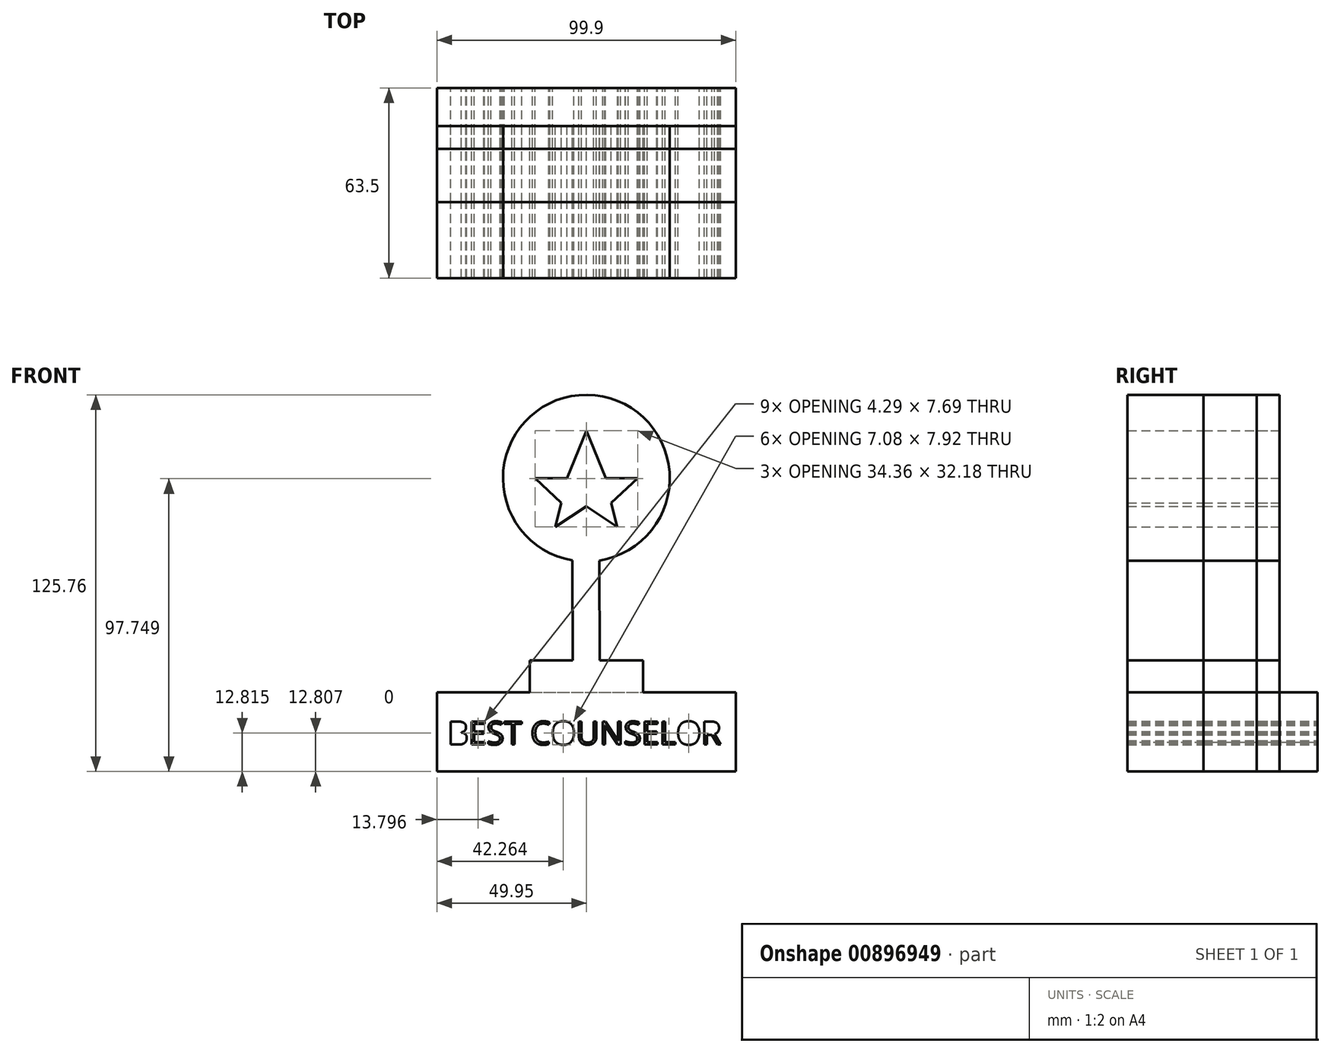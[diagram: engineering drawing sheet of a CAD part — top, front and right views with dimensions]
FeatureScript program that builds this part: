
annotation { "Feature Type Name" : "Feature", "Feature Type Description" : "" }
export const myFeature = defineFeature(function(context is Context, id is Id, definition is map)
    precondition{}
    {
        {
            var Q0;
            Q0=qCreatedBy(makeId("Front.planeOp"),FACE);
            var sketch = newSketch(context, id + "F0", { "sketchPlane" : qUnion([Q0])});
            skArc(sketch, "E0", {"start": v(4.31, 5.18) * mm, "mid": v(0.22, 60.55) * mm, "end": v(-4.75, 5.25) * mm});
            skLineSegment(sketch, "E1.left", {"start": v(-4.75, 5.25) * mm, "end": v(-4.58, -28.13) * mm});
            skLineSegment(sketch, "E1.right", {"start": v(4.31, 5.18) * mm, "end": v(4.48, -28.13) * mm});
            skLineSegment(sketch, "E2.top", {"start": v(-18.91, -28.13) * mm, "end": v(-4.58, -28.13) * mm});
            skLineSegment(sketch, "E2.left", {"start": v(-18.91, -38.77) * mm, "end": v(-18.91, -28.13) * mm});
            skLineSegment(sketch, "E2.right", {"start": v(18.91, -38.77) * mm, "end": v(18.91, -28.13) * mm});
            skLineSegment(sketch, "E3.bottom", {"start": v(-49.95, -38.77) * mm, "end": v(-18.91, -38.77) * mm});
            skLineSegment(sketch, "E3.top", {"start": v(-49.95, -65.21) * mm, "end": v(49.95, -65.21) * mm});
            skLineSegment(sketch, "E3.left", {"start": v(-49.95, -38.77) * mm, "end": v(-49.95, -65.21) * mm});
            skLineSegment(sketch, "E3.right", {"start": v(49.95, -38.77) * mm, "end": v(49.95, -65.21) * mm});
            skPoint(sketch, "E3.middle", {"position": v(0, -52) * mm});
            skLineSegment(sketch, "E4", {"start": v(-122.13, 13.32) * mm, "end": v(-124.07, 16.07) * mm});
            skText(sketch, "E5", { "text": "BEST COUNSELOR\n", "fontName": "OpenSans-Regular.ttf"});
            skLineSegment(sketch, "E6", {"start": v(0, 48.63) * mm, "end": v(6.5, 32.7) * mm});
            skLineSegment(sketch, "E7", {"start": v(6.5, 32.7) * mm, "end": v(17.18, 32.7) * mm});
            skLineSegment(sketch, "E8", {"start": v(17.18, 32.7) * mm, "end": v(8.33, 24.5) * mm});
            skLineSegment(sketch, "E9", {"start": v(8.33, 24.5) * mm, "end": v(10.34, 16.45) * mm});
            skLineSegment(sketch, "E10", {"start": v(0, 60.55) * mm, "end": v(0, 3.64) * mm, "construction": true});
            skPoint(sketch, "E11.start.orphan", {"position": v(-7.83, 32.7) * mm});
            skLineSegment(sketch, "E12.trimOffspring", {"start": v(0, 23.34) * mm, "end": v(10.34, 16.45) * mm});
            skLineSegment(sketch, "E13.MirrorCS", {"start": v(0, 48.63) * mm, "end": v(-6.5, 32.7) * mm});
            skLineSegment(sketch, "E14.MirrorCS", {"start": v(-6.5, 32.7) * mm, "end": v(-17.18, 32.7) * mm});
            skLineSegment(sketch, "E15.MirrorCS", {"start": v(-17.18, 32.7) * mm, "end": v(-8.33, 24.5) * mm});
            skLineSegment(sketch, "E16.MirrorCS", {"start": v(-8.33, 24.5) * mm, "end": v(-10.34, 16.45) * mm});
            skLineSegment(sketch, "E17.MirrorCS", {"start": v(0, 23.34) * mm, "end": v(-10.34, 16.45) * mm});
            skLineSegment(sketch, "E18.trimOffspring", {"start": v(4.48, -28.13) * mm, "end": v(18.91, -28.13) * mm});
            skLineSegment(sketch, "E19.trimOffspring", {"start": v(18.91, -38.77) * mm, "end": v(49.95, -38.77) * mm});
            skLineSegment(sketch, "E20", {"start": v(-4.75, 5.25) * mm, "end": v(4.31, 5.18) * mm});
            skLineSegment(sketch, "E21", {"start": v(-4.58, -28.13) * mm, "end": v(4.48, -28.13) * mm});
            skLineSegment(sketch, "E22", {"start": v(-18.91, -38.77) * mm, "end": v(18.91, -38.77) * mm});
            const initialGuessF0  = {"E5": [-0.04634, -0.05625, 1, 0, 0.00776]};
            skSetInitialGuess(sketch, initialGuessF0);
            skSolve(sketch);
        }
        {
            var Q0;
            Q0=makeQuery(id+"F0.imprint","IMPRINT",FACE,{"disambiguationData":[TD([[makeQuery(id+"F0.imprint","IMPRINT",EDGE,{"derivedFrom":sQuery(id+"F0.wireOp",EDGE,"E3.top")}),1.0]])]});
            extrude(context, id + "F1", {"entities" : qUnion([Q0]), "endBound" : BoundingType.SYMMETRIC, "depth" : 25.4 * mm, "offsetDistance" : 25.4 * mm});
        }
        {
            var Q0;
            Q0=makeQuery(id+"F0.imprint","IMPRINT",FACE,{"disambiguationData":[TD([[makeQuery(id+"F0.imprint","IMPRINT",EDGE,{"derivedFrom":sQuery(id+"F0.wireOp",EDGE,"E2.top")}),-1.0]])]});
            var Q1;
            Q1=makeQuery(id+"F0.imprint","IMPRINT",FACE,{"disambiguationData":[TD([[makeQuery(id+"F0.imprint","IMPRINT",EDGE,{"derivedFrom":sQuery(id+"F0.wireOp",EDGE,"E1.top")}),1.0]])]});
            var Q2;
            Q2=makeQuery(id+"F0.imprint","IMPRINT",FACE,{"disambiguationData":[TD([[makeQuery(id+"F0.imprint","IMPRINT",EDGE,{"derivedFrom":sQuery(id+"F0.wireOp",EDGE,"E6")}),1.0]])]});
            extrude(context, id + "F2", {"entities" : qUnion([Q0, Q1, Q2]), "operationType" : NewBodyOperationType.ADD, "depth" : 12.7 * mm, "offsetDistance" : 25.4 * mm});
        }
        {
            var Q0;
            Q0=makeQuery(id+"F0.imprint","IMPRINT",FACE,{"disambiguationData":[TD([[makeQuery(id+"F0.imprint","IMPRINT",EDGE,{"derivedFrom":sQuery(id+"F0.wireOp",EDGE,"E0")}),1.0]])]});
            extrude(context, id + "F3", {"entities" : qUnion([Q0]), "operationType" : NewBodyOperationType.ADD, "depth" : 25.4 * mm, "offsetDistance" : 25.4 * mm});
        }
        {
            var Q0;
            Q0=qCreatedBy(makeId("Front.planeOp"),FACE);
            var sketch = newSketch(context, id + "F4", { "sketchPlane" : qUnion([Q0])});
            skSolve(sketch);
        }
        {
            var Q0;
            Q0 = qSketchRegion(id + "F4", true);
            var Q1;
            Q1 = qSketchRegion(id + "F0", true);
            extrude(context, id + "F5", {"entities" : qUnion([Q0, Q1]), "operationType" : NewBodyOperationType.ADD, "depth" : 25.4 * mm, "offsetDistance" : 25.4 * mm});
        }
        {
            var Q0;
            Q0 = qSketchRegion(id + "F0", true);
            extrude(context, id + "F6", {"entities" : qUnion([Q0]), "depth" : 7.62 * mm, "offsetDistance" : 25.4 * mm});
        }
        {
            var Q0;
            Q0=makeQuery(id+"F5.opExtrude","CAP_FACE",FACE,{"disambiguationData":[OSD([sQuery(id+"F0.wireOp",EDGE,"E0"),sQuery(id+"F0.wireOp",EDGE,"E1.left"),sQuery(id+"F0.wireOp",EDGE,"E1.right"),sQuery(id+"F0.wireOp",EDGE,"E2.top"),sQuery(id+"F0.wireOp",EDGE,"E2.left"),sQuery(id+"F0.wireOp",EDGE,"E2.right"),sQuery(id+"F0.wireOp",EDGE,"E3.bottom"),sQuery(id+"F0.wireOp",EDGE,"E3.top"),sQuery(id+"F0.wireOp",EDGE,"E3.left"),sQuery(id+"F0.wireOp",EDGE,"E3.right"),sQuery(id+"F0.wireOp",EDGE,"E5.sketch_text.stroke-0"),sQuery(id+"F0.wireOp",EDGE,"E5.sketch_text.stroke-1"),sQuery(id+"F0.wireOp",EDGE,"E5.sketch_text.stroke-2"),sQuery(id+"F0.wireOp",EDGE,"E5.sketch_text.stroke-3"),sQuery(id+"F0.wireOp",EDGE,"E5.sketch_text.stroke-4"),sQuery(id+"F0.wireOp",EDGE,"E5.sketch_text.stroke-5"),sQuery(id+"F0.wireOp",EDGE,"E5.sketch_text.stroke-6"),sQuery(id+"F0.wireOp",EDGE,"E5.sketch_text.stroke-7"),sQuery(id+"F0.wireOp",EDGE,"E5.sketch_text.stroke-8"),sQuery(id+"F0.wireOp",EDGE,"E5.sketch_text.stroke-9"),sQuery(id+"F0.wireOp",EDGE,"E5.sketch_text.stroke-10"),sQuery(id+"F0.wireOp",EDGE,"E5.sketch_text.stroke-25"),sQuery(id+"F0.wireOp",EDGE,"E5.sketch_text.stroke-26"),sQuery(id+"F0.wireOp",EDGE,"E5.sketch_text.stroke-27"),sQuery(id+"F0.wireOp",EDGE,"E5.sketch_text.stroke-28"),sQuery(id+"F0.wireOp",EDGE,"E5.sketch_text.stroke-29"),sQuery(id+"F0.wireOp",EDGE,"E5.sketch_text.stroke-30"),sQuery(id+"F0.wireOp",EDGE,"E5.sketch_text.stroke-31"),sQuery(id+"F0.wireOp",EDGE,"E5.sketch_text.stroke-32"),sQuery(id+"F0.wireOp",EDGE,"E5.sketch_text.stroke-33"),sQuery(id+"F0.wireOp",EDGE,"E5.sketch_text.stroke-34"),sQuery(id+"F0.wireOp",EDGE,"E5.sketch_text.stroke-35"),sQuery(id+"F0.wireOp",EDGE,"E5.sketch_text.stroke-36"),sQuery(id+"F0.wireOp",EDGE,"E5.sketch_text.stroke-37"),sQuery(id+"F0.wireOp",EDGE,"E5.sketch_text.stroke-38"),sQuery(id+"F0.wireOp",EDGE,"E5.sketch_text.stroke-39"),sQuery(id+"F0.wireOp",EDGE,"E5.sketch_text.stroke-40"),sQuery(id+"F0.wireOp",EDGE,"E5.sketch_text.stroke-41"),sQuery(id+"F0.wireOp",EDGE,"E5.sketch_text.stroke-42"),sQuery(id+"F0.wireOp",EDGE,"E5.sketch_text.stroke-43"),sQuery(id+"F0.wireOp",EDGE,"E5.sketch_text.stroke-44"),sQuery(id+"F0.wireOp",EDGE,"E5.sketch_text.stroke-45"),sQuery(id+"F0.wireOp",EDGE,"E5.sketch_text.stroke-46"),sQuery(id+"F0.wireOp",EDGE,"E5.sketch_text.stroke-47"),sQuery(id+"F0.wireOp",EDGE,"E5.sketch_text.stroke-48"),sQuery(id+"F0.wireOp",EDGE,"E5.sketch_text.stroke-49"),sQuery(id+"F0.wireOp",EDGE,"E5.sketch_text.stroke-50"),sQuery(id+"F0.wireOp",EDGE,"E5.sketch_text.stroke-51"),sQuery(id+"F0.wireOp",EDGE,"E5.sketch_text.stroke-52"),sQuery(id+"F0.wireOp",EDGE,"E5.sketch_text.stroke-53"),sQuery(id+"F0.wireOp",EDGE,"E5.sketch_text.stroke-54"),sQuery(id+"F0.wireOp",EDGE,"E5.sketch_text.stroke-55"),sQuery(id+"F0.wireOp",EDGE,"E5.sketch_text.stroke-56"),sQuery(id+"F0.wireOp",EDGE,"E5.sketch_text.stroke-57"),sQuery(id+"F0.wireOp",EDGE,"E5.sketch_text.stroke-58"),sQuery(id+"F0.wireOp",EDGE,"E5.sketch_text.stroke-59"),sQuery(id+"F0.wireOp",EDGE,"E5.sketch_text.stroke-60"),sQuery(id+"F0.wireOp",EDGE,"E5.sketch_text.stroke-61"),sQuery(id+"F0.wireOp",EDGE,"E5.sketch_text.stroke-62"),sQuery(id+"F0.wireOp",EDGE,"E5.sketch_text.stroke-63"),sQuery(id+"F0.wireOp",EDGE,"E5.sketch_text.stroke-64"),sQuery(id+"F0.wireOp",EDGE,"E5.sketch_text.stroke-65"),sQuery(id+"F0.wireOp",EDGE,"E5.sketch_text.stroke-66"),sQuery(id+"F0.wireOp",EDGE,"E5.sketch_text.stroke-67"),sQuery(id+"F0.wireOp",EDGE,"E5.sketch_text.stroke-68"),sQuery(id+"F0.wireOp",EDGE,"E5.sketch_text.stroke-69"),sQuery(id+"F0.wireOp",EDGE,"E5.sketch_text.stroke-70"),sQuery(id+"F0.wireOp",EDGE,"E5.sketch_text.stroke-71"),sQuery(id+"F0.wireOp",EDGE,"E5.sketch_text.stroke-72"),sQuery(id+"F0.wireOp",EDGE,"E5.sketch_text.stroke-73"),sQuery(id+"F0.wireOp",EDGE,"E5.sketch_text.stroke-74"),sQuery(id+"F0.wireOp",EDGE,"E5.sketch_text.stroke-75"),sQuery(id+"F0.wireOp",EDGE,"E5.sketch_text.stroke-76"),sQuery(id+"F0.wireOp",EDGE,"E5.sketch_text.stroke-77"),sQuery(id+"F0.wireOp",EDGE,"E5.sketch_text.stroke-78"),sQuery(id+"F0.wireOp",EDGE,"E5.sketch_text.stroke-79"),sQuery(id+"F0.wireOp",EDGE,"E5.sketch_text.stroke-80"),sQuery(id+"F0.wireOp",EDGE,"E5.sketch_text.stroke-81"),sQuery(id+"F0.wireOp",EDGE,"E5.sketch_text.stroke-82"),sQuery(id+"F0.wireOp",EDGE,"E5.sketch_text.stroke-83"),sQuery(id+"F0.wireOp",EDGE,"E5.sketch_text.stroke-84"),sQuery(id+"F0.wireOp",EDGE,"E5.sketch_text.stroke-85"),sQuery(id+"F0.wireOp",EDGE,"E5.sketch_text.stroke-86"),sQuery(id+"F0.wireOp",EDGE,"E5.sketch_text.stroke-87"),sQuery(id+"F0.wireOp",EDGE,"E5.sketch_text.stroke-88"),sQuery(id+"F0.wireOp",EDGE,"E5.sketch_text.stroke-89"),sQuery(id+"F0.wireOp",EDGE,"E5.sketch_text.stroke-90"),sQuery(id+"F0.wireOp",EDGE,"E5.sketch_text.stroke-91"),sQuery(id+"F0.wireOp",EDGE,"E5.sketch_text.stroke-92"),sQuery(id+"F0.wireOp",EDGE,"E5.sketch_text.stroke-101"),sQuery(id+"F0.wireOp",EDGE,"E5.sketch_text.stroke-102"),sQuery(id+"F0.wireOp",EDGE,"E5.sketch_text.stroke-103"),sQuery(id+"F0.wireOp",EDGE,"E5.sketch_text.stroke-104"),sQuery(id+"F0.wireOp",EDGE,"E5.sketch_text.stroke-105"),sQuery(id+"F0.wireOp",EDGE,"E5.sketch_text.stroke-106"),sQuery(id+"F0.wireOp",EDGE,"E5.sketch_text.stroke-107"),sQuery(id+"F0.wireOp",EDGE,"E5.sketch_text.stroke-108"),sQuery(id+"F0.wireOp",EDGE,"E5.sketch_text.stroke-109"),sQuery(id+"F0.wireOp",EDGE,"E5.sketch_text.stroke-110"),sQuery(id+"F0.wireOp",EDGE,"E5.sketch_text.stroke-111"),sQuery(id+"F0.wireOp",EDGE,"E5.sketch_text.stroke-112"),sQuery(id+"F0.wireOp",EDGE,"E5.sketch_text.stroke-113"),sQuery(id+"F0.wireOp",EDGE,"E5.sketch_text.stroke-114"),sQuery(id+"F0.wireOp",EDGE,"E5.sketch_text.stroke-115"),sQuery(id+"F0.wireOp",EDGE,"E5.sketch_text.stroke-116"),sQuery(id+"F0.wireOp",EDGE,"E5.sketch_text.stroke-117"),sQuery(id+"F0.wireOp",EDGE,"E5.sketch_text.stroke-118"),sQuery(id+"F0.wireOp",EDGE,"E5.sketch_text.stroke-119"),sQuery(id+"F0.wireOp",EDGE,"E5.sketch_text.stroke-120"),sQuery(id+"F0.wireOp",EDGE,"E5.sketch_text.stroke-121"),sQuery(id+"F0.wireOp",EDGE,"E5.sketch_text.stroke-122"),sQuery(id+"F0.wireOp",EDGE,"E5.sketch_text.stroke-123"),sQuery(id+"F0.wireOp",EDGE,"E5.sketch_text.stroke-124"),sQuery(id+"F0.wireOp",EDGE,"E5.sketch_text.stroke-125"),sQuery(id+"F0.wireOp",EDGE,"E5.sketch_text.stroke-126"),sQuery(id+"F0.wireOp",EDGE,"E5.sketch_text.stroke-127"),sQuery(id+"F0.wireOp",EDGE,"E5.sketch_text.stroke-128"),sQuery(id+"F0.wireOp",EDGE,"E5.sketch_text.stroke-129"),sQuery(id+"F0.wireOp",EDGE,"E5.sketch_text.stroke-130"),sQuery(id+"F0.wireOp",EDGE,"E5.sketch_text.stroke-131"),sQuery(id+"F0.wireOp",EDGE,"E5.sketch_text.stroke-132"),sQuery(id+"F0.wireOp",EDGE,"E5.sketch_text.stroke-133"),sQuery(id+"F0.wireOp",EDGE,"E5.sketch_text.stroke-134"),sQuery(id+"F0.wireOp",EDGE,"E5.sketch_text.stroke-135"),sQuery(id+"F0.wireOp",EDGE,"E5.sketch_text.stroke-136"),sQuery(id+"F0.wireOp",EDGE,"E5.sketch_text.stroke-137"),sQuery(id+"F0.wireOp",EDGE,"E5.sketch_text.stroke-138"),sQuery(id+"F0.wireOp",EDGE,"E5.sketch_text.stroke-139"),sQuery(id+"F0.wireOp",EDGE,"E5.sketch_text.stroke-140"),sQuery(id+"F0.wireOp",EDGE,"E5.sketch_text.stroke-141"),sQuery(id+"F0.wireOp",EDGE,"E5.sketch_text.stroke-142"),sQuery(id+"F0.wireOp",EDGE,"E5.sketch_text.stroke-143"),sQuery(id+"F0.wireOp",EDGE,"E5.sketch_text.stroke-144"),sQuery(id+"F0.wireOp",EDGE,"E5.sketch_text.stroke-145"),sQuery(id+"F0.wireOp",EDGE,"E5.sketch_text.stroke-146"),sQuery(id+"F0.wireOp",EDGE,"E5.sketch_text.stroke-147"),sQuery(id+"F0.wireOp",EDGE,"E5.sketch_text.stroke-148"),sQuery(id+"F0.wireOp",EDGE,"E5.sketch_text.stroke-149"),sQuery(id+"F0.wireOp",EDGE,"E5.sketch_text.stroke-150"),sQuery(id+"F0.wireOp",EDGE,"E5.sketch_text.stroke-151"),sQuery(id+"F0.wireOp",EDGE,"E5.sketch_text.stroke-152"),sQuery(id+"F0.wireOp",EDGE,"E5.sketch_text.stroke-153"),sQuery(id+"F0.wireOp",EDGE,"E5.sketch_text.stroke-154"),sQuery(id+"F0.wireOp",EDGE,"E5.sketch_text.stroke-155"),sQuery(id+"F0.wireOp",EDGE,"E5.sketch_text.stroke-156"),sQuery(id+"F0.wireOp",EDGE,"E5.sketch_text.stroke-157"),sQuery(id+"F0.wireOp",EDGE,"E5.sketch_text.stroke-158"),sQuery(id+"F0.wireOp",EDGE,"E5.sketch_text.stroke-159"),sQuery(id+"F0.wireOp",EDGE,"E5.sketch_text.stroke-160"),sQuery(id+"F0.wireOp",EDGE,"E5.sketch_text.stroke-161"),sQuery(id+"F0.wireOp",EDGE,"E5.sketch_text.stroke-162"),sQuery(id+"F0.wireOp",EDGE,"E5.sketch_text.stroke-163"),sQuery(id+"F0.wireOp",EDGE,"E5.sketch_text.stroke-164"),sQuery(id+"F0.wireOp",EDGE,"E5.sketch_text.stroke-165"),sQuery(id+"F0.wireOp",EDGE,"E5.sketch_text.stroke-166"),sQuery(id+"F0.wireOp",EDGE,"E5.sketch_text.stroke-167"),sQuery(id+"F0.wireOp",EDGE,"E5.sketch_text.stroke-168"),sQuery(id+"F0.wireOp",EDGE,"E5.sketch_text.stroke-169"),sQuery(id+"F0.wireOp",EDGE,"E5.sketch_text.stroke-170"),sQuery(id+"F0.wireOp",EDGE,"E5.sketch_text.stroke-171"),sQuery(id+"F0.wireOp",EDGE,"E5.sketch_text.stroke-172"),sQuery(id+"F0.wireOp",EDGE,"E5.sketch_text.stroke-173"),sQuery(id+"F0.wireOp",EDGE,"E5.sketch_text.stroke-174"),sQuery(id+"F0.wireOp",EDGE,"E5.sketch_text.stroke-175"),sQuery(id+"F0.wireOp",EDGE,"E5.sketch_text.stroke-176"),sQuery(id+"F0.wireOp",EDGE,"E5.sketch_text.stroke-177"),sQuery(id+"F0.wireOp",EDGE,"E5.sketch_text.stroke-178"),sQuery(id+"F0.wireOp",EDGE,"E5.sketch_text.stroke-179"),sQuery(id+"F0.wireOp",EDGE,"E5.sketch_text.stroke-180"),sQuery(id+"F0.wireOp",EDGE,"E5.sketch_text.stroke-189"),sQuery(id+"F0.wireOp",EDGE,"E5.sketch_text.stroke-190"),sQuery(id+"F0.wireOp",EDGE,"E5.sketch_text.stroke-191"),sQuery(id+"F0.wireOp",EDGE,"E5.sketch_text.stroke-192"),sQuery(id+"F0.wireOp",EDGE,"E5.sketch_text.stroke-193"),sQuery(id+"F0.wireOp",EDGE,"E5.sketch_text.stroke-194"),sQuery(id+"F0.wireOp",EDGE,"E5.sketch_text.stroke-195"),sQuery(id+"F0.wireOp",EDGE,"E5.sketch_text.stroke-196"),sQuery(id+"F0.wireOp",EDGE,"E5.sketch_text.stroke-197"),sQuery(id+"F0.wireOp",EDGE,"E5.sketch_text.stroke-198"),sQuery(id+"F0.wireOp",EDGE,"E5.sketch_text.stroke-199"),sQuery(id+"F0.wireOp",EDGE,"E6"),sQuery(id+"F0.wireOp",EDGE,"E7"),sQuery(id+"F0.wireOp",EDGE,"E8"),sQuery(id+"F0.wireOp",EDGE,"E9"),sQuery(id+"F0.wireOp",EDGE,"E12.trimOffspring"),sQuery(id+"F0.wireOp",EDGE,"E13.MirrorCS"),sQuery(id+"F0.wireOp",EDGE,"E14.MirrorCS"),sQuery(id+"F0.wireOp",EDGE,"E15.MirrorCS"),sQuery(id+"F0.wireOp",EDGE,"E16.MirrorCS"),sQuery(id+"F0.wireOp",EDGE,"E17.MirrorCS"),sQuery(id+"F0.wireOp",EDGE,"E18.trimOffspring"),sQuery(id+"F0.wireOp",EDGE,"E19.trimOffspring")])],"isStart":false});
            extrude(context, id + "F7", {"entities" : qUnion([Q0]), "depth" : 25.4 * mm, "offsetDistance" : 25.4 * mm});
        }
    });
